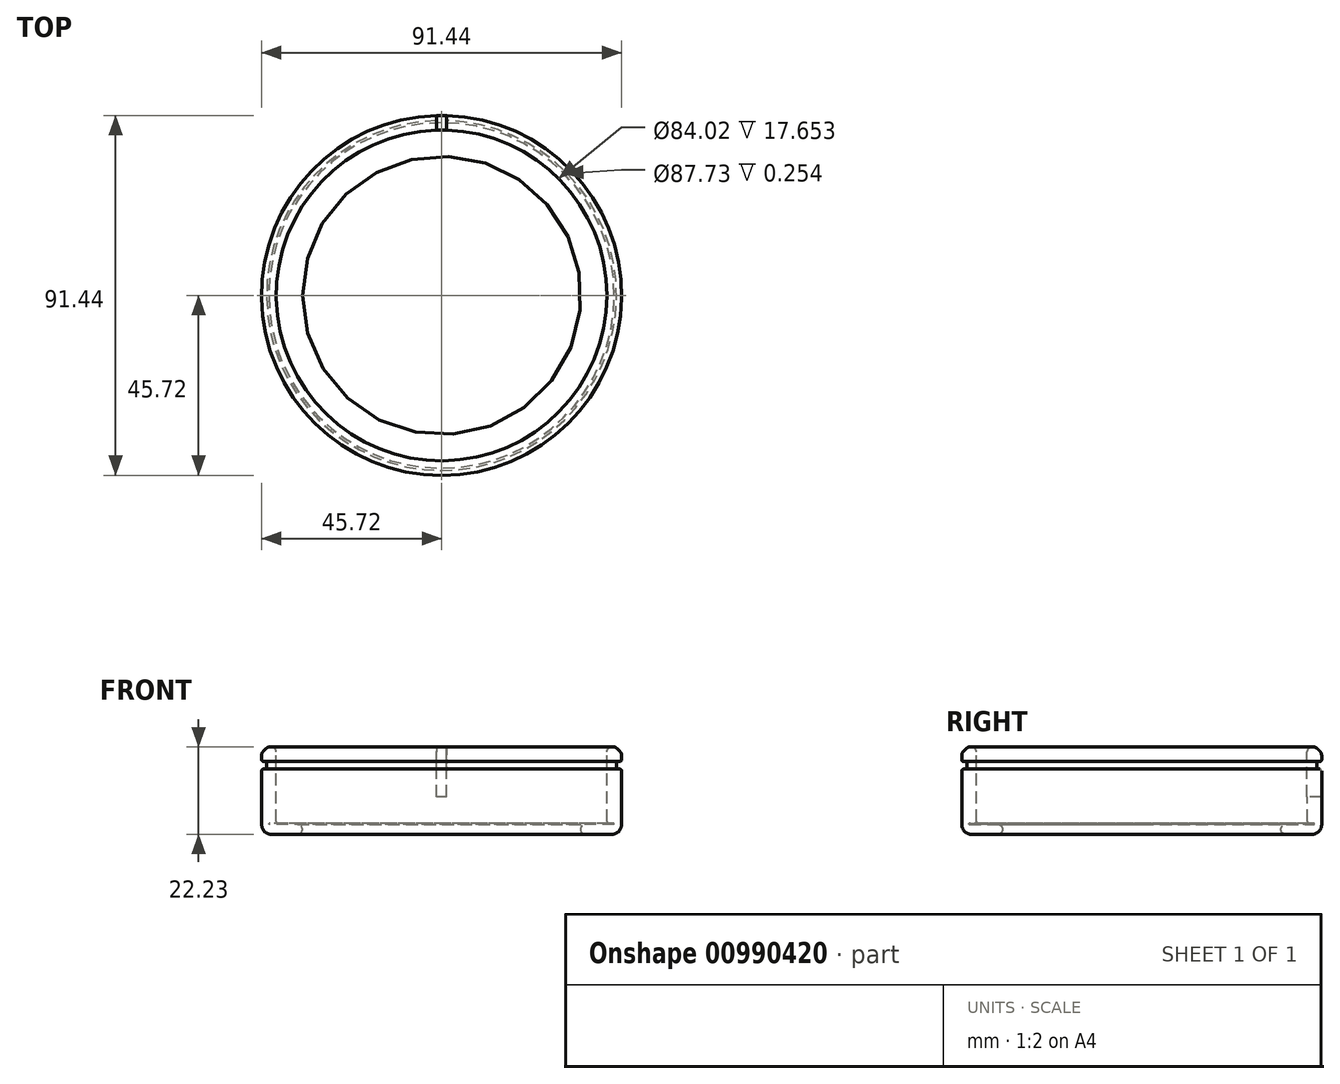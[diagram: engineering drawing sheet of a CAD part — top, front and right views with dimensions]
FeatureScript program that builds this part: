
annotation { "Feature Type Name" : "Feature", "Feature Type Description" : "" }
export const myFeature = defineFeature(function(context is Context, id is Id, definition is map)
    precondition{}
    {
        {
            var Q0;
            Q0=qCreatedBy(makeId("Front.planeOp"),FACE);
            var sketch = newSketch(context, id + "F0", { "sketchPlane" : qUnion([Q0])});
            skLineSegment(sketch, "E0", {"start": v(0, 22.22) * mm, "end": v(0, 0) * mm, "construction": true});
            skLineSegment(sketch, "E1", {"start": v(35.37, 0) * mm, "end": v(45.72, 0) * mm});
            skLineSegment(sketch, "E2", {"start": v(45.72, 0) * mm, "end": v(45.72, 16.61) * mm});
            skLineSegment(sketch, "E3", {"start": v(45.72, 16.61) * mm, "end": v(44.45, 16.61) * mm});
            skLineSegment(sketch, "E4", {"start": v(44.45, 16.61) * mm, "end": v(44.45, 18.52) * mm});
            skLineSegment(sketch, "E5", {"start": v(44.45, 18.52) * mm, "end": v(45.72, 18.52) * mm});
            skLineSegment(sketch, "E6", {"start": v(45.72, 18.52) * mm, "end": v(45.72, 20.69) * mm});
            skLineSegment(sketch, "E7", {"start": v(45.72, 20.69) * mm, "end": v(44.18, 22.23) * mm});
            skLineSegment(sketch, "E8", {"start": v(44.18, 22.23) * mm, "end": v(42.01, 22.23) * mm});
            skLineSegment(sketch, "E9", {"start": v(42.01, 22.23) * mm, "end": v(42.01, 2.8) * mm});
            skLineSegment(sketch, "E10", {"start": v(42.01, 2.8) * mm, "end": v(43.87, 2.8) * mm});
            skLineSegment(sketch, "E11", {"start": v(43.87, 2.8) * mm, "end": v(43.87, 2.54) * mm});
            skLineSegment(sketch, "E12", {"start": v(43.87, 2.54) * mm, "end": v(35.37, 2.54) * mm});
            skLineSegment(sketch, "E13", {"start": v(35.37, 2.54) * mm, "end": v(35.37, 0) * mm});
            skLineSegment(sketch, "E14", {"start": v(43.87, 2.8) * mm, "end": v(45.72, 2.8) * mm, "construction": true});
            skSolve(sketch);
        }
        {
            var Q0;
            Q0 = qSketchRegion(id + "F0", true);
            var Q1;
            Q1=sQuery(id+"F0.wireOp",EDGE,"E0");
            revolve(context, id + "F1", {"surfaceOperationType" : NewSurfaceOperationType.NEW, "entities" : qUnion([Q0]), "axis" : qUnion([Q1]), "revolveType" : RevolveType.FULL});
        }
        {
            var Q0;
            Q0=makeQuery(id+"F1.opRevolve","SWEPT_FACE",FACE,{"disambiguationData":[OSD([sQuery(id+"F0.wireOp",EDGE,"E8")])]});
            var sketch = newSketch(context, id + "F2", { "sketchPlane" : qUnion([Q0])});
            skLineSegment(sketch, "E15.bottom", {"start": v(-1.27, 45.72) * mm, "end": v(1.27, 45.72) * mm});
            skLineSegment(sketch, "E15.top", {"start": v(-1.27, 42) * mm, "end": v(1.27, 42) * mm});
            skLineSegment(sketch, "E15.left", {"start": v(-1.27, 45.72) * mm, "end": v(-1.27, 42) * mm});
            skLineSegment(sketch, "E15.right", {"start": v(1.27, 45.72) * mm, "end": v(1.27, 42) * mm});
            skLineSegment(sketch, "E16", {"start": v(0, 0) * mm, "end": v(0, 45.72) * mm, "construction": true});
            skSolve(sketch);
        }
        {
            var Q0;
            Q0 = qSketchRegion(id + "F2", true);
            extrude(context, id + "F3", {"entities" : qUnion([Q0]), "operationType" : NewBodyOperationType.REMOVE, "oppositeDirection" : true, "depth" : 12.7 * mm, "offsetDistance" : 25.4 * mm});
        }
        {
            var Q0;
            Q0=makeQuery(id+"F1.opRevolve","SWEPT_EDGE",EDGE,{"disambiguationData":[OSD([sQuery(id+"F0.wireOp",EDGE,"E4"),sQuery(id+"F0.wireOp",EDGE,"E5")])]});
            var Q1;
            Q1=makeQuery(id+"F1.opRevolve","SWEPT_EDGE",EDGE,{"disambiguationData":[OSD([sQuery(id+"F0.wireOp",EDGE,"E3"),sQuery(id+"F0.wireOp",EDGE,"E4")])]});
            var Q2;
            Q2=makeQuery(id+"F1.opRevolve","SWEPT_EDGE",EDGE,{"disambiguationData":[OSD([sQuery(id+"F0.wireOp",EDGE,"E2"),sQuery(id+"F0.wireOp",EDGE,"E3")])]});
            var Q3;
            Q3=makeQuery(id+"F1.opRevolve","SWEPT_EDGE",EDGE,{"disambiguationData":[OSD([sQuery(id+"F0.wireOp",EDGE,"E5"),sQuery(id+"F0.wireOp",EDGE,"E6")])]});
            var Q4;
            Q4=makeQuery(id+"F1.opRevolve","SWEPT_EDGE",EDGE,{"disambiguationData":[OSD([sQuery(id+"F0.wireOp",EDGE,"E9"),sQuery(id+"F0.wireOp",EDGE,"E10")])]});
            fillet(context, id + "F4", {"entities" : qUnion([Q0, Q1, Q2, Q3, Q4]), "radius" : 0.5 * mm, "tangentPropagation" : true, "allowEdgeOverflow" : false});
        }
        {
            var Q0;
            Q0=makeQuery(id+"F1.opRevolve","SWEPT_EDGE",EDGE,{"disambiguationData":[OSD([sQuery(id+"F0.wireOp",EDGE,"E6"),sQuery(id+"F0.wireOp",EDGE,"E7")])]});
            var Q1;
            Q1=makeQuery(id+"F1.opRevolve","SWEPT_EDGE",EDGE,{"disambiguationData":[OSD([sQuery(id+"F0.wireOp",EDGE,"E7"),sQuery(id+"F0.wireOp",EDGE,"E8")])]});
            var Q2;
            Q2=makeQuery(id+"F1.opRevolve","SWEPT_EDGE",EDGE,{"disambiguationData":[OSD([sQuery(id+"F0.wireOp",EDGE,"E12"),sQuery(id+"F0.wireOp",EDGE,"E13")])]});
            var Q3;
            Q3=makeQuery(id+"F1.opRevolve","SWEPT_EDGE",EDGE,{"disambiguationData":[OSD([sQuery(id+"F0.wireOp",EDGE,"E1"),sQuery(id+"F0.wireOp",EDGE,"E13")])]});
            var Q4;
            Q4=makeQuery(id+"F1.opRevolve","SWEPT_EDGE",EDGE,{"disambiguationData":[OSD([sQuery(id+"F0.wireOp",EDGE,"E8"),sQuery(id+"F0.wireOp",EDGE,"E9")])]});
            fillet(context, id + "F5", {"entities" : qUnion([Q0, Q1, Q2, Q3, Q4]), "radius" : 1.27 * mm, "tangentPropagation" : true, "allowEdgeOverflow" : false});
        }
        {
            var Q0;
            Q0=makeQuery(id+"F1.opRevolve","SWEPT_EDGE",EDGE,{"disambiguationData":[OSD([sQuery(id+"F0.wireOp",EDGE,"E1"),sQuery(id+"F0.wireOp",EDGE,"E2")])]});
            fillet(context, id + "F6", {"entities" : qUnion([Q0]), "radius" : 2.54 * mm, "tangentPropagation" : true, "allowEdgeOverflow" : false});
        }
    });
